# Revit family: WaterConditioner_ION_SB03-SB19
name_source: partatom
category: Mechanical Equipment
revit_build: Autodesk Revit 2014 (Build: 20130308_1515(x64)
units: mm (PartAtom-declared; Revit-internal decimal feet)

## types (5) — shared parameters
Assembly Code = D2020300
Density_Water_20_ION = 998.2000 kg/m³
Issue_Date_ION = 01/07/15
Issue_Rev_ION = A
Manufacturer = ION Enterprises
URL = www.scalebuster.com
UnitConvert_Area = 1 m²

## per-type parameters (varying)
| type | Equipment_Dia_ION | Equipment_Length_ION | UnitConvert_PressureFactor | UnitSize | Water_ConnectionDia_ION | Weight_Dry_ION |
| SB19 | 32 mm | 157 mm  [stored 0.515092 ft] | 23261435 | KeywayBody : SB19 | 20 mm | 0.70 kg |
| SB12 | 25 mm  [stored 0.082021 ft] | 120 mm  [stored 0.393701 ft] | 199805634 | KeywayBody : SB12 | 15 mm | 0.35 kg |
| SB07 | 25 mm  [stored 0.082021 ft] | 100 mm  [stored 0.328084 ft] | 162292126 | KeywayBody : SB07 | 15 mm | 0.30 kg |
| SB06 | 25 mm  [stored 0.082021 ft] | 100 mm  [stored 0.328084 ft] | 324584252 | KeywayBody : SB06 | 15 mm | 0.30 kg |
| SB03 | 25 mm  [stored 0.082021 ft] | 100 mm  [stored 0.328084 ft] | 5193348026 | KeywayBody : SB03 | 15 mm | 0.30 kg |

note: column(s) folded — value = type name in every type: Model

note: [stored X ft] marks values corroborated as IEEE doubles in the binary element streams (Revit-internal decimal feet)

## geometry (parser evidence)
native form markers: Sweep x4
no freeform markers — native parametric forms only
